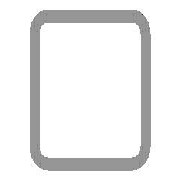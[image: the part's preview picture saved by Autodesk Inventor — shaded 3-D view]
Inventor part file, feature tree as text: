
AUTODESK INVENTOR PART (.ipt)
format: ipt  version: 2025.1 (Build 291241020, 241B)  size: 152,064 bytes
history: native  units: mm (DEFAULTED — no unit token found)
features: other x4, plane x3, split x2, sketch x1
ambient origin geometry x8: Origin, YZ Plane, XZ Plane, XY Plane, X Axis, Y Axis, Z Axis, Center Point
bodies: Solid1 (feature_tree), Body (feature_tree)
feature tree (10):
  parser-record x1  (decoder bookkeeping rows leaked as tree rows — omitted from the tree; the rows remain in map.json)
  other  "Driven Length"
  other  "Start Plane"
  other  "End Plane"
  plane  "Work Plane4"
  split  "Split1"
  plane  "Work Plane5"
  split  "Split2"
  sketch  "Sketch3"  dims[d3=2498.305192mm d4=0.0mm d7=6.0mm d9=80.0mm d11=80.0mm d12=3.0mm d13=-80.0mm d14=2418.305192mm d15=40.0mm d16=40.0mm d17=90.0deg d18=2498.305192mm]
  plane  "Work Plane3"
